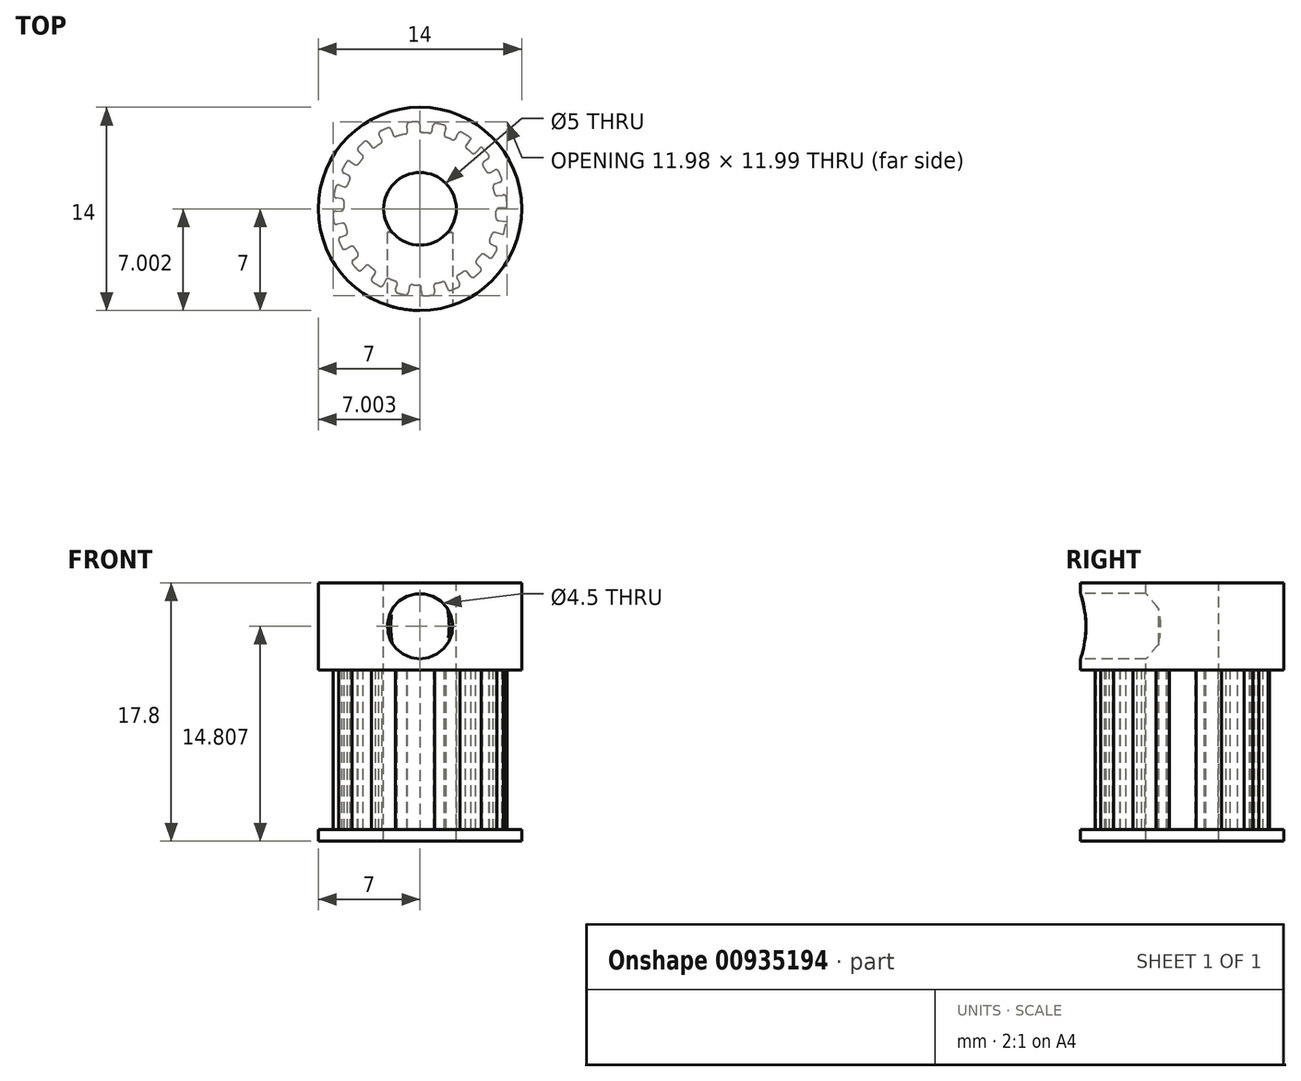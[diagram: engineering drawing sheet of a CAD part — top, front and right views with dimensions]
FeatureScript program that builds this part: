
annotation { "Feature Type Name" : "Feature", "Feature Type Description" : "" }
export const myFeature = defineFeature(function(context is Context, id is Id, definition is map)
    precondition{}
    {
        {
            var Q0;
            Q0=qCreatedBy(makeId("Front.planeOp"),FACE);
            cPlane(context, id + "F0", {"entities" : qUnion([Q0]), "cplaneType" : CPlaneType.OFFSET, "offset" : 7 * mm, "width" : 150 * mm, "height" : 150 * mm});
        }
        {
            var Q0;
            Q0=qCreatedBy(makeId("Top.planeOp"),FACE);
            cPlane(context, id + "F1", {"entities" : qUnion([Q0]), "cplaneType" : CPlaneType.OFFSET, "offset" : 11 * mm, "oppositeDirection" : true, "width" : 150 * mm, "height" : 150 * mm});
        }
        {
            var Q0;
            Q0=qCreatedBy(makeId("Top.planeOp"),FACE);
            var sketch = newSketch(context, id + "F2", { "sketchPlane" : qUnion([Q0])});
            skCircle(sketch, "E0", {"center": v(0, 0) * mm, "radius": 7 * mm});
            skSolve(sketch);
        }
        {
            var Q0;
            Q0=makeQuery(id+"F2.imprint","IMPRINT",FACE,{"disambiguationData":[TD([[makeQuery(id+"F2.imprint","IMPRINT",EDGE,{"derivedFrom":sQuery(id+"F2.wireOp",EDGE,"E0")}),1.0]])]});
            extrude(context, id + "F3", {"entities" : qUnion([Q0]), "depth" : 6 * mm, "offsetDistance" : 25 * mm});
        }
        {
            var Q0;
            Q0=qCreatedBy(makeId("Top.planeOp"),FACE);
            var sketch = newSketch(context, id + "F4", { "sketchPlane" : qUnion([Q0])});
            skCircle(sketch, "E1", {"center": v(0, 0) * mm, "radius": 2.5 * mm});
            skLineSegment(sketch, "E2", {"start": v(-0.82, 5.19) * mm, "end": v(-0.94, 5.93) * mm});
            skArc(sketch, "E3", {"start": v(0, 6) * mm, "mid": v(-0.47, 5.99) * mm, "end": v(-0.94, 5.93) * mm});
            skLineSegment(sketch, "E4", {"start": v(0, 6) * mm, "end": v(0, 5.25) * mm});
            skLineSegment(sketch, "E5.1.0", {"start": v(1.84, 5.7) * mm, "end": v(1.61, 5) * mm});
            skArc(sketch, "E5.1.1", {"start": v(1.84, 5.7) * mm, "mid": v(1.4, 5.84) * mm, "end": v(0.93, 5.93) * mm});
            skLineSegment(sketch, "E5.1.2", {"start": v(0.81, 5.19) * mm, "end": v(0.93, 5.93) * mm});
            skLineSegment(sketch, "E5.2.0", {"start": v(3.5, 4.87) * mm, "end": v(3.07, 4.26) * mm});
            skArc(sketch, "E5.2.1", {"start": v(3.5, 4.87) * mm, "mid": v(3.12, 5.13) * mm, "end": v(2.7, 5.36) * mm});
            skLineSegment(sketch, "E5.2.2", {"start": v(2.37, 4.69) * mm, "end": v(2.7, 5.36) * mm});
            skLineSegment(sketch, "E5.3.0", {"start": v(4.83, 3.55) * mm, "end": v(4.23, 3.1) * mm});
            skArc(sketch, "E5.3.1", {"start": v(4.83, 3.55) * mm, "mid": v(4.54, 3.92) * mm, "end": v(4.22, 4.27) * mm});
            skLineSegment(sketch, "E5.3.2", {"start": v(3.7, 3.73) * mm, "end": v(4.22, 4.27) * mm});
            skLineSegment(sketch, "E5.4.0", {"start": v(5.7, 1.9) * mm, "end": v(4.98, 1.66) * mm});
            skArc(sketch, "E5.4.1", {"start": v(5.7, 1.9) * mm, "mid": v(5.53, 2.34) * mm, "end": v(5.33, 2.76) * mm});
            skLineSegment(sketch, "E5.4.2", {"start": v(4.66, 2.42) * mm, "end": v(5.33, 2.76) * mm});
            skLineSegment(sketch, "E5.5.0", {"start": v(6, 0.06) * mm, "end": v(5.25, 0.05) * mm});
            skArc(sketch, "E5.5.1", {"start": v(6, 0.06) * mm, "mid": v(5.98, 0.53) * mm, "end": v(5.92, 1) * mm});
            skLineSegment(sketch, "E5.5.2", {"start": v(5.18, 0.87) * mm, "end": v(5.92, 1) * mm});
            skLineSegment(sketch, "E5.6.0", {"start": v(5.73, -1.8) * mm, "end": v(5.01, -1.57) * mm});
            skArc(sketch, "E5.6.1", {"start": v(5.73, -1.8) * mm, "mid": v(5.85, -1.34) * mm, "end": v(5.94, -0.87) * mm});
            skLineSegment(sketch, "E5.6.2", {"start": v(5.2, -0.76) * mm, "end": v(5.94, -0.87) * mm});
            skLineSegment(sketch, "E5.7.0", {"start": v(4.9, -3.46) * mm, "end": v(4.29, -3.03) * mm});
            skArc(sketch, "E5.7.1", {"start": v(4.9, -3.46) * mm, "mid": v(5.16, -3.07) * mm, "end": v(5.38, -2.65) * mm});
            skLineSegment(sketch, "E5.7.2", {"start": v(4.7, -2.32) * mm, "end": v(5.38, -2.65) * mm});
            skLineSegment(sketch, "E5.8.0", {"start": v(3.6, -4.8) * mm, "end": v(3.15, -4.2) * mm});
            skArc(sketch, "E5.8.1", {"start": v(3.6, -4.8) * mm, "mid": v(3.97, -4.5) * mm, "end": v(4.3, -4.18) * mm});
            skLineSegment(sketch, "E5.8.2", {"start": v(3.77, -3.66) * mm, "end": v(4.3, -4.18) * mm});
            skLineSegment(sketch, "E5.9.0", {"start": v(1.95, -5.67) * mm, "end": v(1.7, -4.97) * mm});
            skArc(sketch, "E5.9.1", {"start": v(1.95, -5.67) * mm, "mid": v(2.39, -5.5) * mm, "end": v(2.81, -5.3) * mm});
            skLineSegment(sketch, "E5.9.2", {"start": v(2.46, -4.64) * mm, "end": v(2.81, -5.3) * mm});
            skLineSegment(sketch, "E5.10.0", {"start": v(0.11, -6) * mm, "end": v(0.1, -5.25) * mm});
            skArc(sketch, "E5.10.1", {"start": v(0.11, -6) * mm, "mid": v(0.58, -5.98) * mm, "end": v(1.05, -5.9) * mm});
            skLineSegment(sketch, "E5.10.2", {"start": v(0.92, -5.17) * mm, "end": v(1.05, -5.9) * mm});
            skLineSegment(sketch, "E5.11.0", {"start": v(-1.74, -5.74) * mm, "end": v(-1.52, -5.02) * mm});
            skArc(sketch, "E5.11.1", {"start": v(-1.74, -5.74) * mm, "mid": v(-1.28, -5.86) * mm, "end": v(-0.82, -5.94) * mm});
            skLineSegment(sketch, "E5.11.2", {"start": v(-0.72, -5.2) * mm, "end": v(-0.82, -5.94) * mm});
            skLineSegment(sketch, "E5.12.0", {"start": v(-3.42, -4.93) * mm, "end": v(-3, -4.31) * mm});
            skArc(sketch, "E5.12.1", {"start": v(-3.42, -4.93) * mm, "mid": v(-3.02, -5.19) * mm, "end": v(-2.6, -5.4) * mm});
            skLineSegment(sketch, "E5.12.2", {"start": v(-2.28, -4.73) * mm, "end": v(-2.6, -5.4) * mm});
            skLineSegment(sketch, "E5.13.0", {"start": v(-4.77, -3.64) * mm, "end": v(-4.17, -3.19) * mm});
            skArc(sketch, "E5.13.1", {"start": v(-4.77, -3.64) * mm, "mid": v(-4.47, -4) * mm, "end": v(-4.14, -4.34) * mm});
            skLineSegment(sketch, "E5.13.2", {"start": v(-3.62, -3.8) * mm, "end": v(-4.14, -4.34) * mm});
            skLineSegment(sketch, "E5.14.0", {"start": v(-5.66, -2) * mm, "end": v(-4.95, -1.75) * mm});
            skArc(sketch, "E5.14.1", {"start": v(-5.66, -2) * mm, "mid": v(-5.49, -2.44) * mm, "end": v(-5.27, -2.86) * mm});
            skLineSegment(sketch, "E5.14.2", {"start": v(-4.61, -2.5) * mm, "end": v(-5.27, -2.86) * mm});
            skLineSegment(sketch, "E5.15.0", {"start": v(-6, -0.17) * mm, "end": v(-5.25, -0.14) * mm});
            skArc(sketch, "E5.15.1", {"start": v(-6, -0.17) * mm, "mid": v(-5.97, -0.64) * mm, "end": v(-5.9, -1.1) * mm});
            skLineSegment(sketch, "E5.15.2", {"start": v(-5.16, -0.96) * mm, "end": v(-5.9, -1.1) * mm});
            skLineSegment(sketch, "E5.16.0", {"start": v(-5.76, 1.69) * mm, "end": v(-5.04, 1.47) * mm});
            skArc(sketch, "E5.16.1", {"start": v(-5.76, 1.69) * mm, "mid": v(-5.88, 1.23) * mm, "end": v(-5.95, 0.76) * mm});
            skLineSegment(sketch, "E5.16.2", {"start": v(-5.2, 0.67) * mm, "end": v(-5.95, 0.76) * mm});
            skLineSegment(sketch, "E5.17.0", {"start": v(-4.96, 3.37) * mm, "end": v(-4.34, 2.95) * mm});
            skArc(sketch, "E5.17.1", {"start": v(-4.96, 3.37) * mm, "mid": v(-5.21, 2.98) * mm, "end": v(-5.43, 2.56) * mm});
            skLineSegment(sketch, "E5.17.2", {"start": v(-4.75, 2.24) * mm, "end": v(-5.43, 2.56) * mm});
            skLineSegment(sketch, "E5.18.0", {"start": v(-3.69, 4.73) * mm, "end": v(-3.22, 4.14) * mm});
            skArc(sketch, "E5.18.1", {"start": v(-3.69, 4.73) * mm, "mid": v(-4.05, 4.43) * mm, "end": v(-4.38, 4.1) * mm});
            skLineSegment(sketch, "E5.18.2", {"start": v(-3.83, 3.59) * mm, "end": v(-4.38, 4.1) * mm});
            skLineSegment(sketch, "E5.19.0", {"start": v(-2.05, 5.64) * mm, "end": v(-1.8, 4.93) * mm});
            skArc(sketch, "E5.19.1", {"start": v(-2.05, 5.64) * mm, "mid": v(-2.49, 5.46) * mm, "end": v(-2.9, 5.25) * mm});
            skLineSegment(sketch, "E5.19.2", {"start": v(-2.55, 4.6) * mm, "end": v(-2.9, 5.25) * mm});
            skLineSegment(sketch, "E5.anchor1", {"start": v(0, 0) * mm, "end": v(-0.08, 1) * mm, "construction": true});
            skLineSegment(sketch, "E5.anchor2", {"start": v(0, 0) * mm, "end": v(-0.42, 0.91) * mm, "construction": true});
            skArc(sketch, "E6", {"start": v(-2.28, -4.73) * mm, "mid": v(-1.9, -4.9) * mm, "end": v(-1.52, -5.02) * mm});
            skArc(sketch, "E7.trimOffspring", {"start": v(-0.72, -5.2) * mm, "mid": v(-0.31, -5.24) * mm, "end": v(0.1, -5.25) * mm});
            skArc(sketch, "E8.trimOffspring", {"start": v(0.92, -5.17) * mm, "mid": v(1.31, -5.08) * mm, "end": v(1.7, -4.97) * mm});
            skArc(sketch, "E9.trimOffspring", {"start": v(2.46, -4.64) * mm, "mid": v(2.81, -4.43) * mm, "end": v(3.15, -4.2) * mm});
            skArc(sketch, "E10.trimOffspring", {"start": v(3.77, -3.66) * mm, "mid": v(4.04, -3.35) * mm, "end": v(4.29, -3.03) * mm});
            skArc(sketch, "E11.trimOffspring", {"start": v(4.7, -2.32) * mm, "mid": v(4.87, -1.95) * mm, "end": v(5.01, -1.57) * mm});
            skArc(sketch, "E12.trimOffspring", {"start": v(5.2, -0.76) * mm, "mid": v(5.24, -0.36) * mm, "end": v(5.25, 0.05) * mm});
            skArc(sketch, "E13.trimOffspring", {"start": v(5.18, 0.87) * mm, "mid": v(5.1, 1.27) * mm, "end": v(4.98, 1.66) * mm});
            skArc(sketch, "E14.trimOffspring", {"start": v(4.66, 2.42) * mm, "mid": v(4.46, 2.77) * mm, "end": v(4.23, 3.1) * mm});
            skArc(sketch, "E15.trimOffspring", {"start": v(3.7, 3.73) * mm, "mid": v(3.4, 4) * mm, "end": v(3.07, 4.26) * mm});
            skArc(sketch, "E16.trimOffspring", {"start": v(2.37, 4.69) * mm, "mid": v(2, 4.86) * mm, "end": v(1.61, 5) * mm});
            skArc(sketch, "E17.trimOffspring", {"start": v(0.81, 5.19) * mm, "mid": v(0.4, 5.23) * mm, "end": v(0, 5.25) * mm});
            skArc(sketch, "E18.trimOffspring", {"start": v(-0.82, 5.19) * mm, "mid": v(-1.31, 5.08) * mm, "end": v(-1.8, 4.93) * mm});
            skArc(sketch, "E19.trimOffspring", {"start": v(-2.55, 4.6) * mm, "mid": v(-2.9, 4.38) * mm, "end": v(-3.22, 4.14) * mm});
            skArc(sketch, "E20.trimOffspring", {"start": v(-3.83, 3.59) * mm, "mid": v(-4.1, 3.28) * mm, "end": v(-4.34, 2.95) * mm});
            skArc(sketch, "E21.trimOffspring", {"start": v(-4.75, 2.24) * mm, "mid": v(-4.9, 1.86) * mm, "end": v(-5.04, 1.47) * mm});
            skArc(sketch, "E22.trimOffspring", {"start": v(-5.2, 0.67) * mm, "mid": v(-5.24, 0.26) * mm, "end": v(-5.25, -0.14) * mm});
            skArc(sketch, "E23.trimOffspring", {"start": v(-5.16, -0.96) * mm, "mid": v(-5.07, -1.36) * mm, "end": v(-4.95, -1.75) * mm});
            skArc(sketch, "E24.trimOffspring", {"start": v(-4.61, -2.5) * mm, "mid": v(-4.4, -2.85) * mm, "end": v(-4.17, -3.19) * mm});
            skArc(sketch, "E25.trimOffspring", {"start": v(-3.62, -3.8) * mm, "mid": v(-3.32, -4.07) * mm, "end": v(-3, -4.31) * mm});
            skCircle(sketch, "E26", {"center": v(0, 0) * mm, "radius": 6 * mm});
            skSolve(sketch);
        }
        {
            var Q0;
            Q0=makeQuery(id+"F4.imprint","IMPRINT",FACE,{"disambiguationData":[TD([[makeQuery(id+"F4.imprint","IMPRINT",EDGE,{"derivedFrom":sQuery(id+"F4.wireOp",EDGE,"E1")}),-1.0]])]});
            extrude(context, id + "F5", {"entities" : qUnion([Q0]), "operationType" : NewBodyOperationType.ADD, "oppositeDirection" : true, "depth" : 11 * mm, "offsetDistance" : 25 * mm});
        }
        {
            var Q0;
            Q0=makeQuery(id+"F5.boolean.opBoolean","SPLIT",FACE,{"disambiguationData":[TD([makeQuery(id+"F5.opExtrude","SWEPT_FACE",FACE,{"disambiguationData":[OSD([sQuery(id+"F4.wireOp",EDGE,"E1")])]})])],"derivedFrom":makeQuery(id+"F3.opExtrude","CAP_FACE",FACE,{"disambiguationData":[OSD([sQuery(id+"F2.wireOp",EDGE,"E0")])],"isStart":true})});
            extrude(context, id + "F6", {"entities" : qUnion([Q0]), "operationType" : NewBodyOperationType.REMOVE, "oppositeDirection" : true, "depth" : 25 * mm, "offsetDistance" : 25 * mm});
        }
        {
            var Q0;
            Q0=makeQuery(id+"F5.opExtrude","SWEPT_EDGE",EDGE,{"disambiguationData":[OSD([sQuery(id+"F4.wireOp",EDGE,"E5.14.0"),sQuery(id+"F4.wireOp",EDGE,"E23.trimOffspring")])]});
            var Q1;
            Q1=makeQuery(id+"F5.opExtrude","SWEPT_EDGE",EDGE,{"disambiguationData":[OSD([sQuery(id+"F4.wireOp",EDGE,"E5.15.2"),sQuery(id+"F4.wireOp",EDGE,"E23.trimOffspring")])]});
            var Q2;
            Q2=makeQuery(id+"F5.opExtrude","SWEPT_EDGE",EDGE,{"disambiguationData":[OSD([sQuery(id+"F4.wireOp",EDGE,"E5.14.2"),sQuery(id+"F4.wireOp",EDGE,"E24.trimOffspring")])]});
            var Q3;
            Q3=makeQuery(id+"F5.opExtrude","SWEPT_EDGE",EDGE,{"disambiguationData":[OSD([sQuery(id+"F4.wireOp",EDGE,"E5.15.0"),sQuery(id+"F4.wireOp",EDGE,"E22.trimOffspring")])]});
            var Q4;
            Q4=makeQuery(id+"F5.opExtrude","SWEPT_EDGE",EDGE,{"disambiguationData":[OSD([sQuery(id+"F4.wireOp",EDGE,"E5.16.2"),sQuery(id+"F4.wireOp",EDGE,"E22.trimOffspring")])]});
            var Q5;
            Q5=makeQuery(id+"F5.opExtrude","SWEPT_EDGE",EDGE,{"disambiguationData":[OSD([sQuery(id+"F4.wireOp",EDGE,"E5.17.2"),sQuery(id+"F4.wireOp",EDGE,"E21.trimOffspring")])]});
            var Q6;
            Q6=makeQuery(id+"F5.opExtrude","SWEPT_EDGE",EDGE,{"disambiguationData":[OSD([sQuery(id+"F4.wireOp",EDGE,"E5.18.2"),sQuery(id+"F4.wireOp",EDGE,"E20.trimOffspring")])]});
            var Q7;
            Q7=makeQuery(id+"F5.opExtrude","SWEPT_EDGE",EDGE,{"disambiguationData":[OSD([sQuery(id+"F4.wireOp",EDGE,"E5.16.0"),sQuery(id+"F4.wireOp",EDGE,"E21.trimOffspring")])]});
            var Q8;
            Q8=makeQuery(id+"F5.opExtrude","SWEPT_EDGE",EDGE,{"disambiguationData":[OSD([sQuery(id+"F4.wireOp",EDGE,"E5.17.0"),sQuery(id+"F4.wireOp",EDGE,"E20.trimOffspring")])]});
            var Q9;
            Q9=makeQuery(id+"F5.opExtrude","SWEPT_EDGE",EDGE,{"disambiguationData":[OSD([sQuery(id+"F4.wireOp",EDGE,"E5.18.0"),sQuery(id+"F4.wireOp",EDGE,"E19.trimOffspring")])]});
            var Q10;
            Q10=makeQuery(id+"F5.opExtrude","SWEPT_EDGE",EDGE,{"disambiguationData":[OSD([sQuery(id+"F4.wireOp",EDGE,"E5.19.2"),sQuery(id+"F4.wireOp",EDGE,"E19.trimOffspring")])]});
            var Q11;
            Q11=makeQuery(id+"F5.opExtrude","SWEPT_EDGE",EDGE,{"disambiguationData":[OSD([sQuery(id+"F4.wireOp",EDGE,"E2"),sQuery(id+"F4.wireOp",EDGE,"E18.trimOffspring")])]});
            var Q12;
            Q12=makeQuery(id+"F5.opExtrude","SWEPT_EDGE",EDGE,{"disambiguationData":[OSD([sQuery(id+"F4.wireOp",EDGE,"E5.1.2"),sQuery(id+"F4.wireOp",EDGE,"E17.trimOffspring")])]});
            var Q13;
            Q13=makeQuery(id+"F5.opExtrude","SWEPT_EDGE",EDGE,{"disambiguationData":[OSD([sQuery(id+"F4.wireOp",EDGE,"E5.2.2"),sQuery(id+"F4.wireOp",EDGE,"E16.trimOffspring")])]});
            var Q14;
            Q14=makeQuery(id+"F5.opExtrude","SWEPT_EDGE",EDGE,{"disambiguationData":[OSD([sQuery(id+"F4.wireOp",EDGE,"E5.19.0"),sQuery(id+"F4.wireOp",EDGE,"E18.trimOffspring")])]});
            var Q15;
            Q15=makeQuery(id+"F5.opExtrude","SWEPT_EDGE",EDGE,{"disambiguationData":[OSD([sQuery(id+"F4.wireOp",EDGE,"E4"),sQuery(id+"F4.wireOp",EDGE,"E17.trimOffspring")])]});
            var Q16;
            Q16=makeQuery(id+"F5.opExtrude","SWEPT_EDGE",EDGE,{"disambiguationData":[OSD([sQuery(id+"F4.wireOp",EDGE,"E5.1.0"),sQuery(id+"F4.wireOp",EDGE,"E16.trimOffspring")])]});
            var Q17;
            Q17=makeQuery(id+"F5.opExtrude","SWEPT_EDGE",EDGE,{"disambiguationData":[OSD([sQuery(id+"F4.wireOp",EDGE,"E5.2.0"),sQuery(id+"F4.wireOp",EDGE,"E15.trimOffspring")])]});
            var Q18;
            Q18=makeQuery(id+"F5.opExtrude","SWEPT_EDGE",EDGE,{"disambiguationData":[OSD([sQuery(id+"F4.wireOp",EDGE,"E5.3.2"),sQuery(id+"F4.wireOp",EDGE,"E15.trimOffspring")])]});
            var Q19;
            Q19=makeQuery(id+"F5.opExtrude","SWEPT_EDGE",EDGE,{"disambiguationData":[OSD([sQuery(id+"F4.wireOp",EDGE,"E5.3.0"),sQuery(id+"F4.wireOp",EDGE,"E14.trimOffspring")])]});
            var Q20;
            Q20=makeQuery(id+"F5.opExtrude","SWEPT_EDGE",EDGE,{"disambiguationData":[OSD([sQuery(id+"F4.wireOp",EDGE,"E5.5.2"),sQuery(id+"F4.wireOp",EDGE,"E13.trimOffspring")])]});
            var Q21;
            Q21=makeQuery(id+"F5.opExtrude","SWEPT_EDGE",EDGE,{"disambiguationData":[OSD([sQuery(id+"F4.wireOp",EDGE,"E5.6.2"),sQuery(id+"F4.wireOp",EDGE,"E12.trimOffspring")])]});
            var Q22;
            Q22=makeQuery(id+"F5.opExtrude","SWEPT_EDGE",EDGE,{"disambiguationData":[OSD([sQuery(id+"F4.wireOp",EDGE,"E5.4.2"),sQuery(id+"F4.wireOp",EDGE,"E14.trimOffspring")])]});
            var Q23;
            Q23=makeQuery(id+"F5.opExtrude","SWEPT_EDGE",EDGE,{"disambiguationData":[OSD([sQuery(id+"F4.wireOp",EDGE,"E5.4.0"),sQuery(id+"F4.wireOp",EDGE,"E13.trimOffspring")])]});
            var Q24;
            Q24=makeQuery(id+"F5.opExtrude","SWEPT_EDGE",EDGE,{"disambiguationData":[OSD([sQuery(id+"F4.wireOp",EDGE,"E5.5.0"),sQuery(id+"F4.wireOp",EDGE,"E12.trimOffspring")])]});
            var Q25;
            Q25=makeQuery(id+"F5.opExtrude","SWEPT_EDGE",EDGE,{"disambiguationData":[OSD([sQuery(id+"F4.wireOp",EDGE,"E5.6.0"),sQuery(id+"F4.wireOp",EDGE,"E11.trimOffspring")])]});
            var Q26;
            Q26=makeQuery(id+"F5.opExtrude","SWEPT_EDGE",EDGE,{"disambiguationData":[OSD([sQuery(id+"F4.wireOp",EDGE,"E5.7.2"),sQuery(id+"F4.wireOp",EDGE,"E11.trimOffspring")])]});
            var Q27;
            Q27=makeQuery(id+"F5.opExtrude","SWEPT_EDGE",EDGE,{"disambiguationData":[OSD([sQuery(id+"F4.wireOp",EDGE,"E5.8.2"),sQuery(id+"F4.wireOp",EDGE,"E10.trimOffspring")])]});
            var Q28;
            Q28=makeQuery(id+"F5.opExtrude","SWEPT_EDGE",EDGE,{"disambiguationData":[OSD([sQuery(id+"F4.wireOp",EDGE,"E5.9.2"),sQuery(id+"F4.wireOp",EDGE,"E9.trimOffspring")])]});
            var Q29;
            Q29=makeQuery(id+"F5.opExtrude","SWEPT_EDGE",EDGE,{"disambiguationData":[OSD([sQuery(id+"F4.wireOp",EDGE,"E5.9.0"),sQuery(id+"F4.wireOp",EDGE,"E5.9.1")])]});
            var Q30;
            Q30=makeQuery(id+"F5.opExtrude","SWEPT_EDGE",EDGE,{"disambiguationData":[OSD([sQuery(id+"F4.wireOp",EDGE,"E5.7.0"),sQuery(id+"F4.wireOp",EDGE,"E10.trimOffspring")])]});
            var Q31;
            Q31=makeQuery(id+"F5.opExtrude","SWEPT_EDGE",EDGE,{"disambiguationData":[OSD([sQuery(id+"F4.wireOp",EDGE,"E5.8.0"),sQuery(id+"F4.wireOp",EDGE,"E9.trimOffspring")])]});
            var Q32;
            Q32=makeQuery(id+"F5.opExtrude","SWEPT_EDGE",EDGE,{"disambiguationData":[OSD([sQuery(id+"F4.wireOp",EDGE,"E5.9.0"),sQuery(id+"F4.wireOp",EDGE,"E8.trimOffspring")])]});
            var Q33;
            Q33=makeQuery(id+"F5.opExtrude","SWEPT_EDGE",EDGE,{"disambiguationData":[OSD([sQuery(id+"F4.wireOp",EDGE,"E5.10.0"),sQuery(id+"F4.wireOp",EDGE,"E7.trimOffspring")])]});
            var Q34;
            Q34=makeQuery(id+"F5.opExtrude","SWEPT_EDGE",EDGE,{"disambiguationData":[OSD([sQuery(id+"F4.wireOp",EDGE,"E5.12.2"),sQuery(id+"F4.wireOp",EDGE,"E6")])]});
            var Q35;
            Q35=makeQuery(id+"F5.opExtrude","SWEPT_EDGE",EDGE,{"disambiguationData":[OSD([sQuery(id+"F4.wireOp",EDGE,"E5.10.2"),sQuery(id+"F4.wireOp",EDGE,"E8.trimOffspring")])]});
            var Q36;
            Q36=makeQuery(id+"F5.opExtrude","SWEPT_EDGE",EDGE,{"disambiguationData":[OSD([sQuery(id+"F4.wireOp",EDGE,"E5.11.2"),sQuery(id+"F4.wireOp",EDGE,"E7.trimOffspring")])]});
            var Q37;
            Q37=makeQuery(id+"F5.opExtrude","SWEPT_EDGE",EDGE,{"disambiguationData":[OSD([sQuery(id+"F4.wireOp",EDGE,"E5.11.0"),sQuery(id+"F4.wireOp",EDGE,"E6")])]});
            var Q38;
            Q38=makeQuery(id+"F5.opExtrude","SWEPT_EDGE",EDGE,{"disambiguationData":[OSD([sQuery(id+"F4.wireOp",EDGE,"E5.12.0"),sQuery(id+"F4.wireOp",EDGE,"E25.trimOffspring")])]});
            var Q39;
            Q39=makeQuery(id+"F5.opExtrude","SWEPT_EDGE",EDGE,{"disambiguationData":[OSD([sQuery(id+"F4.wireOp",EDGE,"E5.13.2"),sQuery(id+"F4.wireOp",EDGE,"E25.trimOffspring")])]});
            var Q40;
            Q40=makeQuery(id+"F5.opExtrude","SWEPT_EDGE",EDGE,{"disambiguationData":[OSD([sQuery(id+"F4.wireOp",EDGE,"E5.13.0"),sQuery(id+"F4.wireOp",EDGE,"E24.trimOffspring")])]});
            fillet(context, id + "F7", {"entities" : qUnion([Q0, Q1, Q2, Q3, Q4, Q5, Q6, Q7, Q8, Q9, Q10, Q11, Q12, Q13, Q14, Q15, Q16, Q17, Q18, Q19, Q20, Q21, Q22, Q23, Q24, Q25, Q26, Q27, Q28, Q29, Q30, Q31, Q32, Q33, Q34, Q35, Q36, Q37, Q38, Q39, Q40]), "radius" : 0.2 * mm, "tangentPropagation" : true, "allowEdgeOverflow" : false});
        }
        {
            var Q0;
            Q0=makeQuery(id+"F5.opExtrude","SWEPT_EDGE",EDGE,{"disambiguationData":[OSD([sQuery(id+"F4.wireOp",EDGE,"E5.13.1"),sQuery(id+"F4.wireOp",EDGE,"E5.13.2")])]});
            var Q1;
            Q1=makeQuery(id+"F5.opExtrude","SWEPT_EDGE",EDGE,{"disambiguationData":[OSD([sQuery(id+"F4.wireOp",EDGE,"E5.13.0"),sQuery(id+"F4.wireOp",EDGE,"E5.13.1")])]});
            var Q2;
            Q2=makeQuery(id+"F5.opExtrude","SWEPT_EDGE",EDGE,{"disambiguationData":[OSD([sQuery(id+"F4.wireOp",EDGE,"E5.14.1"),sQuery(id+"F4.wireOp",EDGE,"E5.14.2")])]});
            var Q3;
            Q3=makeQuery(id+"F5.opExtrude","SWEPT_EDGE",EDGE,{"disambiguationData":[OSD([sQuery(id+"F4.wireOp",EDGE,"E5.14.0"),sQuery(id+"F4.wireOp",EDGE,"E5.14.1")])]});
            var Q4;
            Q4=makeQuery(id+"F5.opExtrude","SWEPT_EDGE",EDGE,{"disambiguationData":[OSD([sQuery(id+"F4.wireOp",EDGE,"E5.15.1"),sQuery(id+"F4.wireOp",EDGE,"E5.15.2")])]});
            var Q5;
            Q5=makeQuery(id+"F5.opExtrude","SWEPT_EDGE",EDGE,{"disambiguationData":[OSD([sQuery(id+"F4.wireOp",EDGE,"E5.15.0"),sQuery(id+"F4.wireOp",EDGE,"E5.15.1")])]});
            var Q6;
            Q6=makeQuery(id+"F5.opExtrude","SWEPT_EDGE",EDGE,{"disambiguationData":[OSD([sQuery(id+"F4.wireOp",EDGE,"E5.16.1"),sQuery(id+"F4.wireOp",EDGE,"E5.16.2")])]});
            var Q7;
            Q7=makeQuery(id+"F5.opExtrude","SWEPT_EDGE",EDGE,{"disambiguationData":[OSD([sQuery(id+"F4.wireOp",EDGE,"E5.10.1"),sQuery(id+"F4.wireOp",EDGE,"E5.10.2")])]});
            var Q8;
            Q8=makeQuery(id+"F5.opExtrude","SWEPT_EDGE",EDGE,{"disambiguationData":[OSD([sQuery(id+"F4.wireOp",EDGE,"E5.9.1"),sQuery(id+"F4.wireOp",EDGE,"E5.9.2")])]});
            var Q9;
            Q9=makeQuery(id+"F5.opExtrude","SWEPT_EDGE",EDGE,{"disambiguationData":[OSD([sQuery(id+"F4.wireOp",EDGE,"E5.8.0"),sQuery(id+"F4.wireOp",EDGE,"E5.8.1")])]});
            var Q10;
            Q10=makeQuery(id+"F5.opExtrude","SWEPT_EDGE",EDGE,{"disambiguationData":[OSD([sQuery(id+"F4.wireOp",EDGE,"E5.8.1"),sQuery(id+"F4.wireOp",EDGE,"E5.8.2")])]});
            var Q11;
            Q11=makeQuery(id+"F5.opExtrude","SWEPT_EDGE",EDGE,{"disambiguationData":[OSD([sQuery(id+"F4.wireOp",EDGE,"E5.7.0"),sQuery(id+"F4.wireOp",EDGE,"E5.7.1")])]});
            var Q12;
            Q12=makeQuery(id+"F5.opExtrude","SWEPT_EDGE",EDGE,{"disambiguationData":[OSD([sQuery(id+"F4.wireOp",EDGE,"E5.7.1"),sQuery(id+"F4.wireOp",EDGE,"E5.7.2")])]});
            var Q13;
            Q13=makeQuery(id+"F5.opExtrude","SWEPT_EDGE",EDGE,{"disambiguationData":[OSD([sQuery(id+"F4.wireOp",EDGE,"E5.5.0"),sQuery(id+"F4.wireOp",EDGE,"E5.5.1")])]});
            var Q14;
            Q14=makeQuery(id+"F5.opExtrude","SWEPT_EDGE",EDGE,{"disambiguationData":[OSD([sQuery(id+"F4.wireOp",EDGE,"E5.5.1"),sQuery(id+"F4.wireOp",EDGE,"E5.5.2")])]});
            var Q15;
            Q15=makeQuery(id+"F5.opExtrude","SWEPT_EDGE",EDGE,{"disambiguationData":[OSD([sQuery(id+"F4.wireOp",EDGE,"E5.4.0"),sQuery(id+"F4.wireOp",EDGE,"E5.4.1")])]});
            var Q16;
            Q16=makeQuery(id+"F5.opExtrude","SWEPT_EDGE",EDGE,{"disambiguationData":[OSD([sQuery(id+"F4.wireOp",EDGE,"E5.4.1"),sQuery(id+"F4.wireOp",EDGE,"E5.4.2")])]});
            var Q17;
            Q17=makeQuery(id+"F5.opExtrude","SWEPT_EDGE",EDGE,{"disambiguationData":[OSD([sQuery(id+"F4.wireOp",EDGE,"E5.3.0"),sQuery(id+"F4.wireOp",EDGE,"E5.3.1")])]});
            var Q18;
            Q18=makeQuery(id+"F5.opExtrude","SWEPT_EDGE",EDGE,{"disambiguationData":[OSD([sQuery(id+"F4.wireOp",EDGE,"E5.2.1"),sQuery(id+"F4.wireOp",EDGE,"E5.2.2")])]});
            var Q19;
            Q19=makeQuery(id+"F5.opExtrude","SWEPT_EDGE",EDGE,{"disambiguationData":[OSD([sQuery(id+"F4.wireOp",EDGE,"E5.1.0"),sQuery(id+"F4.wireOp",EDGE,"E5.1.1")])]});
            var Q20;
            Q20=makeQuery(id+"F5.opExtrude","SWEPT_EDGE",EDGE,{"disambiguationData":[OSD([sQuery(id+"F4.wireOp",EDGE,"E5.1.1"),sQuery(id+"F4.wireOp",EDGE,"E5.1.2")])]});
            var Q21;
            Q21=makeQuery(id+"F5.opExtrude","SWEPT_EDGE",EDGE,{"disambiguationData":[OSD([sQuery(id+"F4.wireOp",EDGE,"E3"),sQuery(id+"F4.wireOp",EDGE,"E4")])]});
            var Q22;
            Q22=makeQuery(id+"F5.opExtrude","SWEPT_EDGE",EDGE,{"disambiguationData":[OSD([sQuery(id+"F4.wireOp",EDGE,"E2"),sQuery(id+"F4.wireOp",EDGE,"E3")])]});
            var Q23;
            Q23=makeQuery(id+"F5.opExtrude","SWEPT_EDGE",EDGE,{"disambiguationData":[OSD([sQuery(id+"F4.wireOp",EDGE,"E5.19.0"),sQuery(id+"F4.wireOp",EDGE,"E5.19.1")])]});
            var Q24;
            Q24=makeQuery(id+"F5.opExtrude","SWEPT_EDGE",EDGE,{"disambiguationData":[OSD([sQuery(id+"F4.wireOp",EDGE,"E5.19.1"),sQuery(id+"F4.wireOp",EDGE,"E5.19.2")])]});
            var Q25;
            Q25=makeQuery(id+"F5.opExtrude","SWEPT_EDGE",EDGE,{"disambiguationData":[OSD([sQuery(id+"F4.wireOp",EDGE,"E5.18.0"),sQuery(id+"F4.wireOp",EDGE,"E5.18.1")])]});
            var Q26;
            Q26=makeQuery(id+"F5.opExtrude","SWEPT_EDGE",EDGE,{"disambiguationData":[OSD([sQuery(id+"F4.wireOp",EDGE,"E5.18.1"),sQuery(id+"F4.wireOp",EDGE,"E5.18.2")])]});
            var Q27;
            Q27=makeQuery(id+"F5.opExtrude","SWEPT_EDGE",EDGE,{"disambiguationData":[OSD([sQuery(id+"F4.wireOp",EDGE,"E5.17.0"),sQuery(id+"F4.wireOp",EDGE,"E5.17.1")])]});
            var Q28;
            Q28=makeQuery(id+"F5.opExtrude","SWEPT_EDGE",EDGE,{"disambiguationData":[OSD([sQuery(id+"F4.wireOp",EDGE,"E5.17.1"),sQuery(id+"F4.wireOp",EDGE,"E5.17.2")])]});
            var Q29;
            Q29=makeQuery(id+"F5.opExtrude","SWEPT_EDGE",EDGE,{"disambiguationData":[OSD([sQuery(id+"F4.wireOp",EDGE,"E5.16.0"),sQuery(id+"F4.wireOp",EDGE,"E5.16.1")])]});
            var Q30;
            Q30=makeQuery(id+"F5.opExtrude","SWEPT_EDGE",EDGE,{"disambiguationData":[OSD([sQuery(id+"F4.wireOp",EDGE,"E5.12.0"),sQuery(id+"F4.wireOp",EDGE,"E5.12.1")])]});
            var Q31;
            Q31=makeQuery(id+"F5.opExtrude","SWEPT_EDGE",EDGE,{"disambiguationData":[OSD([sQuery(id+"F4.wireOp",EDGE,"E5.12.1"),sQuery(id+"F4.wireOp",EDGE,"E5.12.2")])]});
            var Q32;
            Q32=makeQuery(id+"F5.opExtrude","SWEPT_EDGE",EDGE,{"disambiguationData":[OSD([sQuery(id+"F4.wireOp",EDGE,"E5.11.0"),sQuery(id+"F4.wireOp",EDGE,"E5.11.1")])]});
            var Q33;
            Q33=makeQuery(id+"F5.opExtrude","SWEPT_EDGE",EDGE,{"disambiguationData":[OSD([sQuery(id+"F4.wireOp",EDGE,"E5.11.1"),sQuery(id+"F4.wireOp",EDGE,"E5.11.2")])]});
            var Q34;
            Q34=makeQuery(id+"F5.opExtrude","SWEPT_EDGE",EDGE,{"disambiguationData":[OSD([sQuery(id+"F4.wireOp",EDGE,"E5.10.0"),sQuery(id+"F4.wireOp",EDGE,"E5.10.1")])]});
            fillet(context, id + "F8", {"entities" : qUnion([Q0, Q1, Q2, Q3, Q4, Q5, Q6, Q7, Q8, Q9, Q10, Q11, Q12, Q13, Q14, Q15, Q16, Q17, Q18, Q19, Q20, Q21, Q22, Q23, Q24, Q25, Q26, Q27, Q28, Q29, Q30, Q31, Q32, Q33, Q34]), "radius" : 0.2 * mm, "tangentPropagation" : true, "allowEdgeOverflow" : false});
        }
        {
            var Q0;
            Q0=qCreatedBy(id+"F1.planeOp",FACE);
            var sketch = newSketch(context, id + "F9", { "sketchPlane" : qUnion([Q0])});
            skCircle(sketch, "E27", {"center": v(0, 0) * mm, "radius": 7 * mm});
            skCircle(sketch, "E28", {"center": v(0, 0) * mm, "radius": 2.5 * mm});
            skSolve(sketch);
        }
        {
            var Q0;
            Q0=makeQuery(id+"F9.imprint","IMPRINT",FACE,{"disambiguationData":[TD([[makeQuery(id+"F9.imprint","IMPRINT",EDGE,{"derivedFrom":sQuery(id+"F9.wireOp",EDGE,"E27")}),1.0]])]});
            extrude(context, id + "F10", {"entities" : qUnion([Q0]), "operationType" : NewBodyOperationType.ADD, "oppositeDirection" : true, "depth" : 0.8 * mm, "offsetDistance" : 25 * mm});
        }
        {
            var Q0;
            Q0=qCreatedBy(id+"F0.planeOp",FACE);
            var sketch = newSketch(context, id + "F11", { "sketchPlane" : qUnion([Q0])});
            skLineSegment(sketch, "E29", {"start": v(0, 6.01) * mm, "end": v(0, 0) * mm, "construction": true});
            skPoint(sketch, "E30", {"position": v(0, 3) * mm});
            skSolve(sketch);
        }
        {
            var Q0;
            Q0=sQuery(id+"F11.wireOp",VERTEX,"E30");
            var Q1;
            Q1=makeQuery(id+"F3.opExtrude","SWEPT_BODY",BODY,{"disambiguationData":[OSD([sQuery(id+"F2.wireOp",EDGE,"E0")])]});
            hole(context, id + "F12", {"style" : HoleStyle.SIMPLE, "endStyle" : HoleEndStyle.BLIND, "standardTappedOrClearance" : lookupTablePath({ "fit" : "Normal", "standard" : "ISO", "size" : "M4", "type" : "Clearance" }), "standardBlindInLast" : lookupTablePath({ "fit" : "Normal", "standard" : "ISO", "size" : "M4", "type" : "Clearance" }), "holeDiameter" : 4.5 * mm, "majorDiameter" : 5 * mm, "holeDepth" : 5 * mm, "tappedDepth" : 12 * mm, "tapClearance" : 3, "locations" : qUnion([Q0]), "scope" : qUnion([Q1])});
        }
    });
